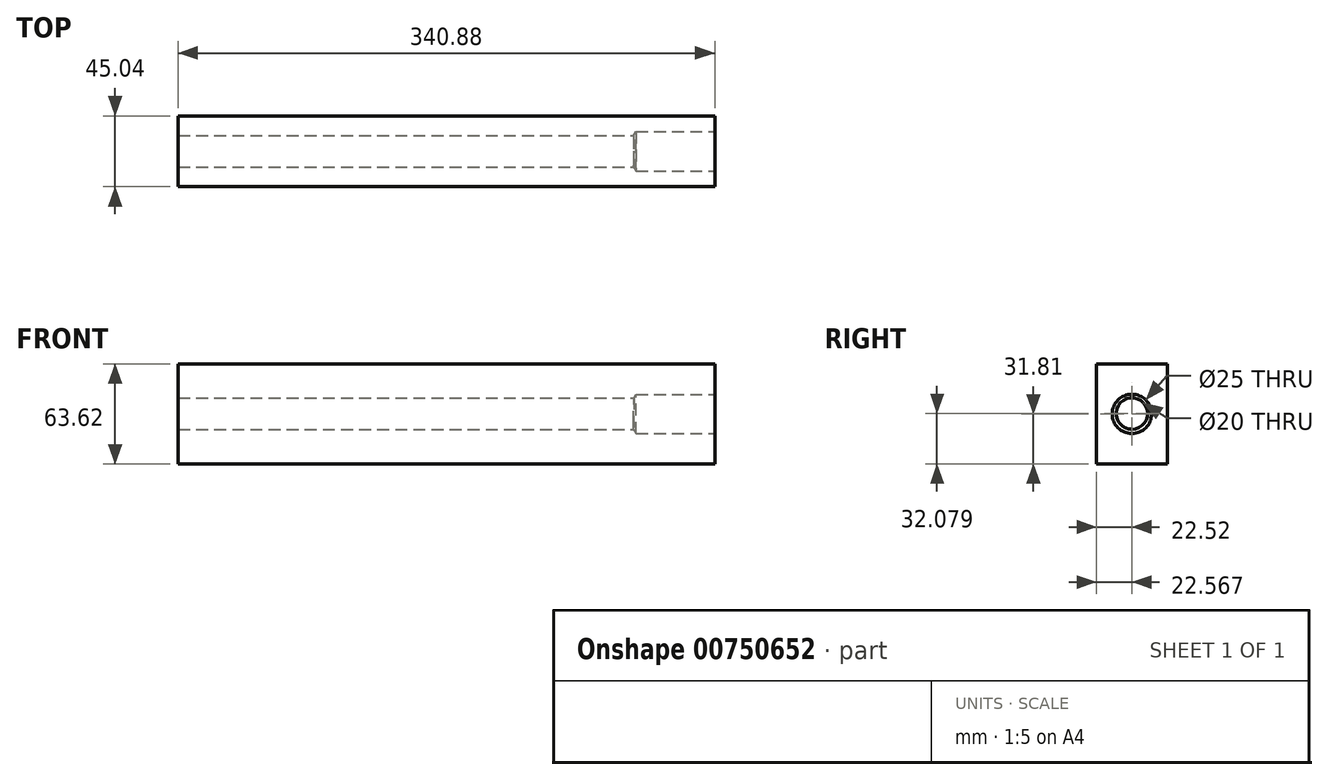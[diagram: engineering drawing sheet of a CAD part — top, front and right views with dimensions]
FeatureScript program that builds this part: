
annotation { "Feature Type Name" : "Feature", "Feature Type Description" : "" }
export const myFeature = defineFeature(function(context is Context, id is Id, definition is map)
    precondition{}
    {
        {
            var Q0;
            Q0=qCreatedBy(makeId("Right.planeOp"),FACE);
            var sketch = newSketch(context, id + "F0", { "sketchPlane" : qUnion([Q0])});
            skLineSegment(sketch, "E0.bottom", {"start": v(22.52, 31.81) * mm, "end": v(-22.52, 31.81) * mm});
            skLineSegment(sketch, "E0.top", {"start": v(22.52, -31.81) * mm, "end": v(-22.52, -31.81) * mm});
            skLineSegment(sketch, "E0.left", {"start": v(22.52, 31.81) * mm, "end": v(22.52, -31.81) * mm});
            skLineSegment(sketch, "E0.right", {"start": v(-22.52, 31.81) * mm, "end": v(-22.52, -31.81) * mm});
            skPoint(sketch, "E0.middle", {"position": v(0, 0) * mm});
            skSolve(sketch);
        }
        {
            var Q0;
            Q0=makeQuery(id+"F0.imprint","IMPRINT",FACE,{"disambiguationData":[TD([[makeQuery(id+"F0.imprint","IMPRINT",EDGE,{"derivedFrom":sQuery(id+"F0.wireOp",EDGE,"E0.bottom")}),1.0]])]});
            extrude(context, id + "F1", {"entities" : qUnion([Q0]), "endBound" : BoundingType.SYMMETRIC, "depth" : 340.88 * mm, "offsetDistance" : 25.4 * mm});
        }
        {
            var Q0;
            Q0=makeQuery(id+"F1.opExtrude","CAP_FACE",FACE,{"disambiguationData":[OSD([sQuery(id+"F0.wireOp",EDGE,"E0.bottom"),sQuery(id+"F0.wireOp",EDGE,"E0.top"),sQuery(id+"F0.wireOp",EDGE,"E0.left"),sQuery(id+"F0.wireOp",EDGE,"E0.right")])],"isStart":false});
            var sketch = newSketch(context, id + "F2", { "sketchPlane" : qUnion([Q0])});
            skCircle(sketch, "E1", {"center": v(0, 0) * mm, "radius": 17.41 * mm});
            skSolve(sketch);
        }
        {
            var Q0;
            Q0=sQuery(id+"F2.wireOp",VERTEX,"E1.center");
            var Q1;
            Q1=makeQuery(id+"F1.opExtrude","SWEPT_BODY",BODY,{"disambiguationData":[OSD([sQuery(id+"F0.wireOp",EDGE,"E0.bottom"),sQuery(id+"F0.wireOp",EDGE,"E0.top"),sQuery(id+"F0.wireOp",EDGE,"E0.left"),sQuery(id+"F0.wireOp",EDGE,"E0.right")])]});
            hole(context, id + "F3", {"style" : HoleStyle.SIMPLE, "endStyle" : HoleEndStyle.BLIND, "holeDiameter" : 25 * mm, "majorDiameter" : 5 * mm, "holeDepth" : 50 * mm, "isTappedThrough" : true, "tappedDepth" : 12 * mm, "tapClearance" : 3, "locations" : qUnion([Q0]), "scope" : qUnion([Q1])});
        }
        {
            var Q0;
            Q0=makeQuery(id+"F1.opExtrude","CAP_FACE",FACE,{"disambiguationData":[OSD([sQuery(id+"F0.wireOp",EDGE,"E0.bottom"),sQuery(id+"F0.wireOp",EDGE,"E0.top"),sQuery(id+"F0.wireOp",EDGE,"E0.left"),sQuery(id+"F0.wireOp",EDGE,"E0.right")])],"isStart":false});
            var sketch = newSketch(context, id + "F4", { "sketchPlane" : qUnion([Q0])});
            skCircle(sketch, "E2", {"center": v(0.05, 0.27) * mm, "radius": 5.56 * mm});
            skSolve(sketch);
        }
        {
            var Q0;
            Q0=sQuery(id+"F4.wireOp",VERTEX,"E2.center");
            var Q1;
            Q1=makeQuery(id+"F1.opExtrude","SWEPT_BODY",BODY,{"disambiguationData":[OSD([sQuery(id+"F0.wireOp",EDGE,"E0.bottom"),sQuery(id+"F0.wireOp",EDGE,"E0.top"),sQuery(id+"F0.wireOp",EDGE,"E0.left"),sQuery(id+"F0.wireOp",EDGE,"E0.right")])]});
            hole(context, id + "F5", {"style" : HoleStyle.SIMPLE, "endStyle" : HoleEndStyle.THROUGH, "holeDiameter" : 20 * mm, "majorDiameter" : 5 * mm, "isTappedThrough" : true, "tappedDepth" : 12 * mm, "tapClearance" : 3, "locations" : qUnion([Q0]), "scope" : qUnion([Q1])});
        }
    });
